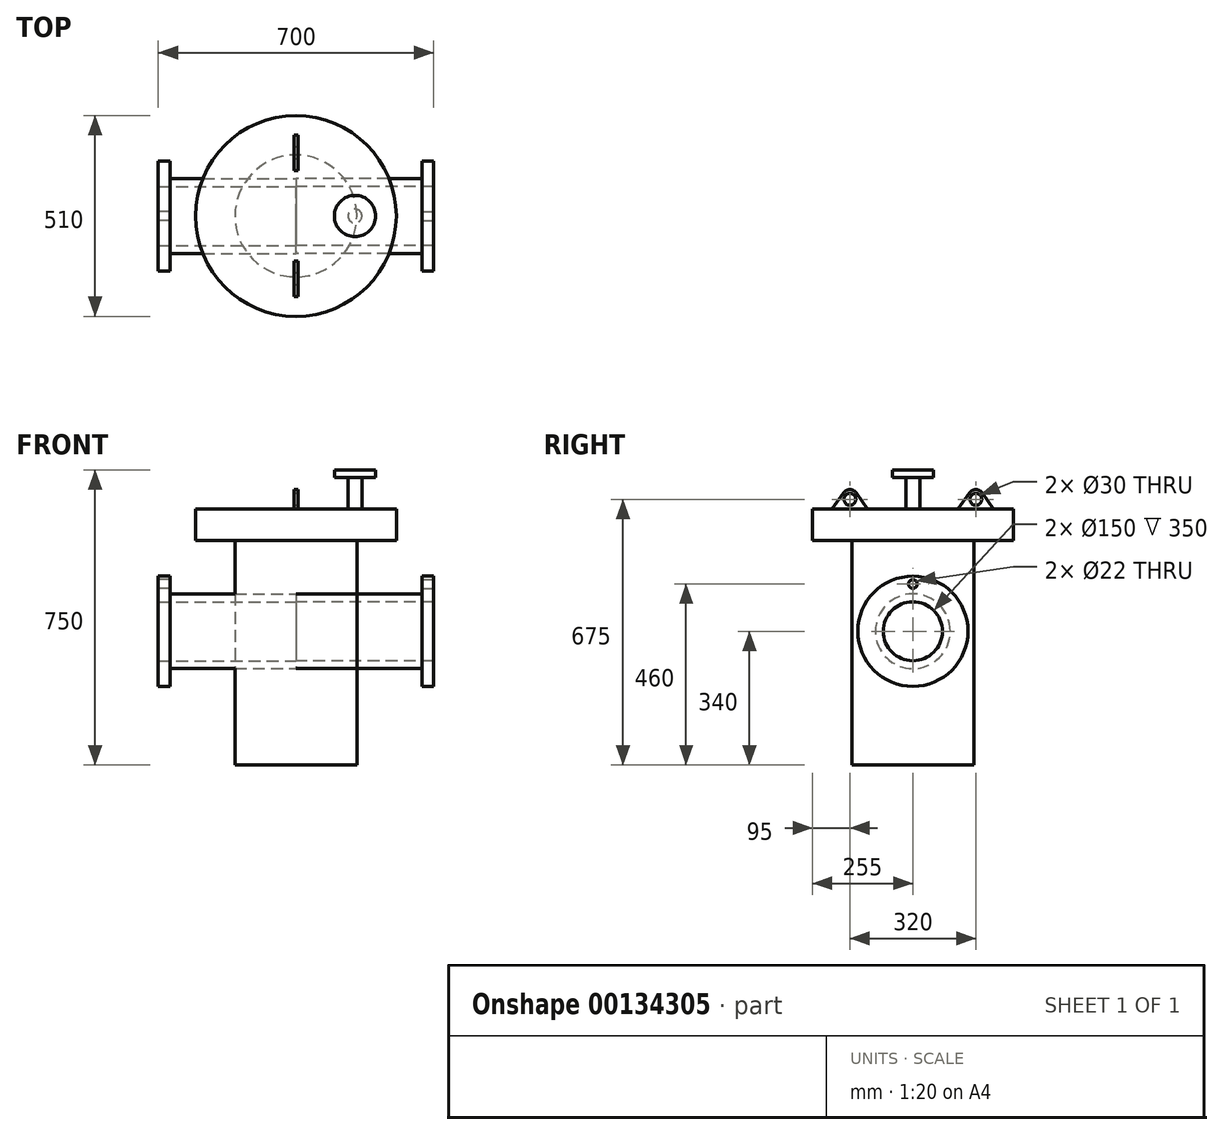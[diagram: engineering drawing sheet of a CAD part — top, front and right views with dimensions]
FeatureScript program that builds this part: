
annotation { "Feature Type Name" : "Feature", "Feature Type Description" : "" }
export const myFeature = defineFeature(function(context is Context, id is Id, definition is map)
    precondition{}
    {
        {
            var Q0;
            Q0=qCreatedBy(makeId("Front.planeOp"),FACE);
            var sketch = newSketch(context, id + "F0", { "sketchPlane" : qUnion([Q0])});
            skLineSegment(sketch, "E0", {"start": v(0, 0) * mm, "end": v(0, -650) * mm});
            skLineSegment(sketch, "E1", {"start": v(0, -650) * mm, "end": v(155, -650) * mm});
            skLineSegment(sketch, "E2", {"start": v(155, -650) * mm, "end": v(155, -80) * mm});
            skLineSegment(sketch, "E3", {"start": v(155, -80) * mm, "end": v(255, -80) * mm});
            skLineSegment(sketch, "E4", {"start": v(255, -80) * mm, "end": v(255, 0) * mm});
            skLineSegment(sketch, "E5", {"start": v(255, 0) * mm, "end": v(0, 0) * mm});
            skLineSegment(sketch, "E6", {"start": v(0, 184.13) * mm, "end": v(0, 397.52) * mm, "construction": true});
            skSolve(sketch);
        }
        {
            var Q0;
            Q0=qCreatedBy(makeId("Front.planeOp"),FACE);
            var sketch = newSketch(context, id + "F1", { "sketchPlane" : qUnion([Q0])});
            skLineSegment(sketch, "E7", {"start": v(150, 0) * mm, "end": v(150, 100) * mm});
            skLineSegment(sketch, "E8", {"start": v(150, 100) * mm, "end": v(202.5, 100) * mm});
            skLineSegment(sketch, "E9", {"start": v(202.5, 100) * mm, "end": v(202.5, 80) * mm});
            skLineSegment(sketch, "E10", {"start": v(202.5, 80) * mm, "end": v(167.5, 80) * mm});
            skLineSegment(sketch, "E11", {"start": v(167.5, 80) * mm, "end": v(167.5, 0) * mm});
            skLineSegment(sketch, "E12", {"start": v(167.5, 0) * mm, "end": v(150, 0) * mm});
            skSolve(sketch);
        }
        {
            var Q0;
            Q0=makeQuery(id+"F1.imprint","IMPRINT",FACE,{"disambiguationData":[TD([[makeQuery(id+"F1.imprint","IMPRINT",EDGE,{"derivedFrom":sQuery(id+"F1.wireOp",EDGE,"E7")}),-1.0]])]});
            var Q1;
            Q1=sQuery(id+"F1.wireOp",EDGE,"E7");
            revolve(context, id + "F2", {"entities" : qUnion([Q0]), "axis" : qUnion([Q1]), "revolveType" : RevolveType.FULL});
        }
        {
            var Q0;
            Q0=qCreatedBy(makeId("Right.planeOp"),FACE);
            var sketch = newSketch(context, id + "F3", { "sketchPlane" : qUnion([Q0])});
            skLineSegment(sketch, "E13", {"start": v(205, 0) * mm, "end": v(115, 0) * mm});
            skLineSegment(sketch, "E14", {"start": v(115, 0) * mm, "end": v(160, 65) * mm});
            skLineSegment(sketch, "E15", {"start": v(205, 0) * mm, "end": v(160, 65) * mm});
            skCircle(sketch, "E16", {"center": v(160, 25) * mm, "radius": 15 * mm});
            skSolve(sketch);
        }
        {
            var Q0;
            Q0=makeQuery(id+"F3.imprint","IMPRINT",FACE,{"disambiguationData":[TD([[makeQuery(id+"F3.imprint","IMPRINT",EDGE,{"derivedFrom":sQuery(id+"F3.wireOp",EDGE,"E13")}),-1.0]])]});
            extrude(context, id + "F4", {"entities" : qUnion([Q0]), "operationType" : NewBodyOperationType.ADD, "endBound" : BoundingType.SYMMETRIC, "depth" : 10 * mm});
        }
        {
            var Q0;
            Q0=makeQuery(id+"F4.opExtrude","SWEPT_EDGE",EDGE,{"disambiguationData":[OSD([sQuery(id+"F3.wireOp",EDGE,"E14"),sQuery(id+"F3.wireOp",EDGE,"E15")])]});
            fillet(context, id + "F5", {"entities" : qUnion([Q0]), "radius" : 20 * mm, "tangentPropagation" : true, "allowEdgeOverflow" : false});
        }
        {
            var Q0;
            Q0=makeQuery(id+"F4.opExtrude","SWEPT_BODY",BODY,{"disambiguationData":[OSD([sQuery(id+"F3.wireOp",EDGE,"E13"),sQuery(id+"F3.wireOp",EDGE,"E14"),sQuery(id+"F3.wireOp",EDGE,"E15"),sQuery(id+"F3.wireOp",EDGE,"E16")])]});
            var Q1;
            Q1=qCreatedBy(makeId("Front.planeOp"),FACE);
            mirror(context, id + "F6", {"entities" : qUnion([Q0]), "mirrorPlane" : qUnion([Q1])});
        }
        {
            var Q0;
            Q0=qCreatedBy(makeId("Front.planeOp"),FACE);
            var sketch = newSketch(context, id + "F7", { "sketchPlane" : qUnion([Q0])});
            skLineSegment(sketch, "E17", {"start": v(350, -235) * mm, "end": v(350, -170) * mm});
            skLineSegment(sketch, "E18", {"start": v(350, -170) * mm, "end": v(320, -170) * mm});
            skLineSegment(sketch, "E19", {"start": v(320, -170) * mm, "end": v(320, -215) * mm});
            skLineSegment(sketch, "E20", {"start": v(320, -215) * mm, "end": v(0, -215) * mm});
            skLineSegment(sketch, "E21", {"start": v(0, -215) * mm, "end": v(0, -235) * mm});
            skLineSegment(sketch, "E22", {"start": v(0, -235) * mm, "end": v(350, -235) * mm});
            skLineSegment(sketch, "E23", {"start": v(0, -310) * mm, "end": v(493.22, -310) * mm, "construction": true});
            skSolve(sketch);
        }
        {
            var Q0;
            Q0=makeQuery(id+"F7.imprint","IMPRINT",FACE,{"disambiguationData":[TD([[makeQuery(id+"F7.imprint","IMPRINT",EDGE,{"derivedFrom":sQuery(id+"F7.wireOp",EDGE,"E17")}),1.0]])]});
            var Q1;
            Q1=sQuery(id+"F7.wireOp",EDGE,"E23");
            revolve(context, id + "F8", {"operationType" : NewBodyOperationType.ADD, "entities" : qUnion([Q0]), "axis" : qUnion([Q1]), "revolveType" : RevolveType.FULL});
        }
        {
            var Q0;
            Q0=makeQuery(id+"F8.opRevolve","SWEPT_FACE",FACE,{"disambiguationData":[OSD([sQuery(id+"F7.wireOp",EDGE,"E17")])]});
            var sketch = newSketch(context, id + "F9", { "sketchPlane" : qUnion([Q0])});
            skCircle(sketch, "E24", {"center": v(0, -190) * mm, "radius": 11 * mm});
            skCircle(sketch, "E25", {"center": v(0, -310) * mm, "radius": 120 * mm, "construction": true});
            skLineSegment(sketch, "E26", {"start": v(0, -310) * mm, "end": v(0, -190) * mm, "construction": true});
            skSolve(sketch);
        }
        {
            var Q0;
            Q0=makeQuery(id+"F9.imprint","IMPRINT",FACE,{"disambiguationData":[TD([[makeQuery(id+"F9.imprint","IMPRINT",EDGE,{"derivedFrom":sQuery(id+"F9.wireOp",EDGE,"E24")}),1.0]])]});
            extrude(context, id + "F10", {"entities" : qUnion([Q0]), "operationType" : NewBodyOperationType.REMOVE, "endBound" : BoundingType.UP_TO_NEXT, "oppositeDirection" : true, "depth" : 50 * mm});
        }
        {
            var Q0;
            Q0=makeQuery(id+"F8.opRevolve","SWEPT_BODY",BODY,{"disambiguationData":[OSD([sQuery(id+"F7.wireOp",EDGE,"E17"),sQuery(id+"F7.wireOp",EDGE,"E18"),sQuery(id+"F7.wireOp",EDGE,"E19"),sQuery(id+"F7.wireOp",EDGE,"E20"),sQuery(id+"F7.wireOp",EDGE,"E21"),sQuery(id+"F7.wireOp",EDGE,"E22")])]});
            var Q1;
            Q1=makeQuery(id+"F10.opExtrude","SWEPT_BODY",BODY,{"disambiguationData":[OSD([sQuery(id+"F9.wireOp",EDGE,"E24")])]});
            var Q2;
            Q2=qCreatedBy(makeId("Right.planeOp"),FACE);
            mirror(context, id + "F11", {"operationType" : NewBodyOperationType.ADD, "entities" : qUnion([Q0, Q1]), "mirrorPlane" : qUnion([Q2])});
        }
        {
            var Q0;
            Q0=makeQuery(id+"F0.imprint","IMPRINT",FACE,{"disambiguationData":[TD([[makeQuery(id+"F0.imprint","IMPRINT",EDGE,{"derivedFrom":sQuery(id+"F0.wireOp",EDGE,"E0")}),1.0]])]});
            var Q1;
            Q1=sQuery(id+"F0.wireOp",EDGE,"E6");
            revolve(context, id + "F12", {"entities" : qUnion([Q0]), "axis" : qUnion([Q1]), "revolveType" : RevolveType.FULL});
        }
    });
